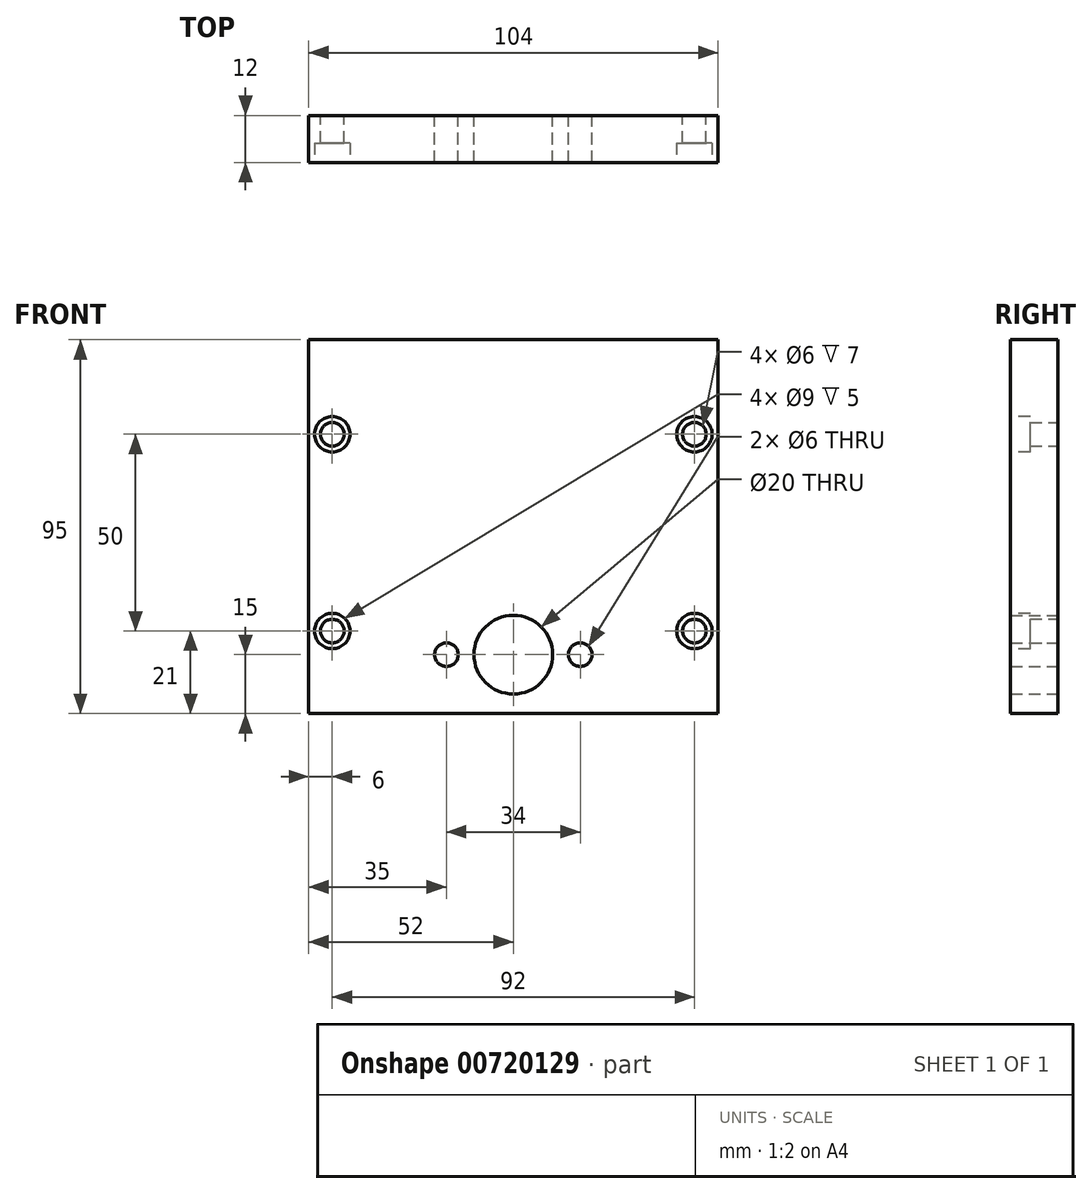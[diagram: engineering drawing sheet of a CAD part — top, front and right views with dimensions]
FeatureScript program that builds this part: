
annotation { "Feature Type Name" : "Feature", "Feature Type Description" : "" }
export const myFeature = defineFeature(function(context is Context, id is Id, definition is map)
    precondition{}
    {
        {
            var Q0;
            Q0=qCreatedBy(makeId("Front.planeOp"),FACE);
            var sketch = newSketch(context, id + "F0", { "sketchPlane" : qUnion([Q0])});
            skLineSegment(sketch, "E0.bottom", {"start": v(0, 0) * mm, "end": v(104, 0) * mm});
            skLineSegment(sketch, "E0.top", {"start": v(0, 95) * mm, "end": v(104, 95) * mm});
            skLineSegment(sketch, "E0.left", {"start": v(0, 0) * mm, "end": v(0, 95) * mm});
            skLineSegment(sketch, "E0.right", {"start": v(104, 0) * mm, "end": v(104, 95) * mm});
            skCircle(sketch, "E1", {"center": v(52, 15) * mm, "radius": 10 * mm});
            skPoint(sketch, "E1.centerSnap0", {"position": v(52, 0) * mm});
            skCircle(sketch, "E2", {"center": v(6, 21) * mm, "radius": 3 * mm});
            skCircle(sketch, "E3", {"center": v(98, 21) * mm, "radius": 3 * mm});
            skCircle(sketch, "E4", {"center": v(6, 71) * mm, "radius": 3 * mm});
            skCircle(sketch, "E5", {"center": v(98, 71) * mm, "radius": 3 * mm});
            skCircle(sketch, "E6", {"center": v(35, 15) * mm, "radius": 3 * mm});
            skCircle(sketch, "E7", {"center": v(69, 15) * mm, "radius": 3 * mm});
            skSolve(sketch);
        }
        {
            var Q0;
            Q0=makeQuery(id+"F0.imprint","IMPRINT",FACE,{"disambiguationData":[TD([[makeQuery(id+"F0.imprint","IMPRINT",EDGE,{"derivedFrom":sQuery(id+"F0.wireOp",EDGE,"E0.bottom")}),1.0]])]});
            extrude(context, id + "F1", {"entities" : qUnion([Q0]), "depth" : 12 * mm, "offsetDistance" : 25 * mm});
        }
        {
            var Q0;
            Q0=makeQuery(id+"F1.opExtrude","CAP_FACE",FACE,{"disambiguationData":[OSD([sQuery(id+"F0.wireOp",EDGE,"E0.bottom"),sQuery(id+"F0.wireOp",EDGE,"E0.top"),sQuery(id+"F0.wireOp",EDGE,"E0.left"),sQuery(id+"F0.wireOp",EDGE,"E0.right"),sQuery(id+"F0.wireOp",EDGE,"E1"),sQuery(id+"F0.wireOp",EDGE,"E2"),sQuery(id+"F0.wireOp",EDGE,"E3"),sQuery(id+"F0.wireOp",EDGE,"E4"),sQuery(id+"F0.wireOp",EDGE,"E5")])],"isStart":false});
            var sketch = newSketch(context, id + "F2", { "sketchPlane" : qUnion([Q0])});
            skCircle(sketch, "E8", {"center": v(6, 71) * mm, "radius": 4.5 * mm});
            skCircle(sketch, "E9", {"center": v(98, 71) * mm, "radius": 4.5 * mm});
            skCircle(sketch, "E10", {"center": v(98, 21) * mm, "radius": 4.5 * mm});
            skCircle(sketch, "E11", {"center": v(6, 21) * mm, "radius": 4.5 * mm});
            skSolve(sketch);
        }
        {
            var Q0;
            Q0 = qSketchRegion(id + "F2", true);
            extrude(context, id + "F3", {"entities" : qUnion([Q0]), "operationType" : NewBodyOperationType.REMOVE, "oppositeDirection" : true, "depth" : 5 * mm, "offsetDistance" : 25 * mm});
        }
    });
